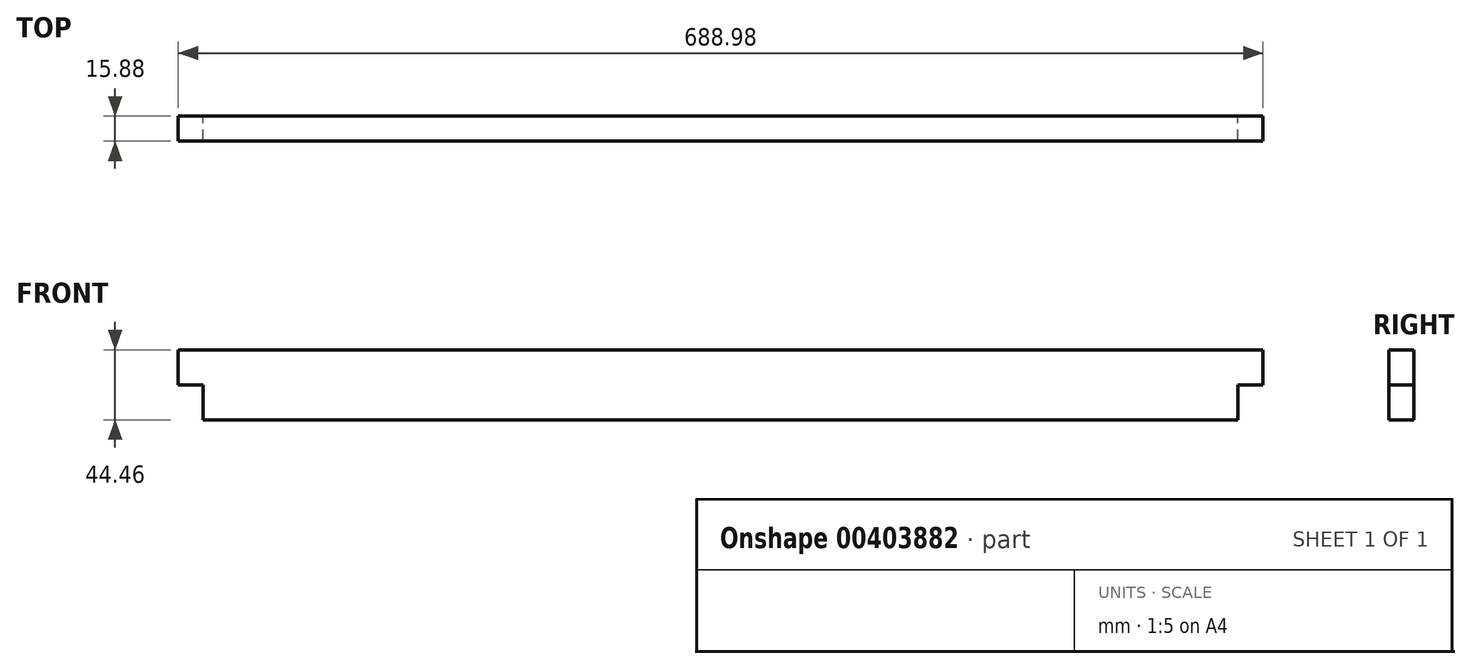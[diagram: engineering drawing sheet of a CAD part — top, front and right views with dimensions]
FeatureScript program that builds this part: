
annotation { "Feature Type Name" : "Feature", "Feature Type Description" : "" }
export const myFeature = defineFeature(function(context is Context, id is Id, definition is map)
    precondition{}
    {
        {
            var Q0;
            Q0=qCreatedBy(makeId("Front.planeOp"),FACE);
            var sketch = newSketch(context, id + "F0", { "sketchPlane" : qUnion([Q0])});
            skLineSegment(sketch, "E0.bottom", {"start": v(344.49, -22.23) * mm, "end": v(-344.49, -22.23) * mm});
            skLineSegment(sketch, "E0.top", {"start": v(344.49, 22.23) * mm, "end": v(-344.49, 22.22) * mm});
            skLineSegment(sketch, "E0.left", {"start": v(344.49, -22.23) * mm, "end": v(344.49, 22.22) * mm});
            skLineSegment(sketch, "E0.right", {"start": v(-344.49, -22.23) * mm, "end": v(-344.49, 22.22) * mm});
            skPoint(sketch, "E0.middle", {"position": v(0, 0) * mm});
            skSolve(sketch);
        }
        {
            var Q0;
            Q0 = qSketchRegion(id + "F0", true);
            extrude(context, id + "F1", {"entities" : qUnion([Q0]), "depth" : 15.88 * mm});
        }
        {
            var Q0;
            Q0=makeQuery(id+"F0.imprint","IMPRINT",FACE,{"disambiguationData":[TD([[makeQuery(id+"F0.imprint","IMPRINT",EDGE,{"derivedFrom":sQuery(id+"F0.wireOp",EDGE,"E0.bottom")}),-1.0]])]});
            var sketch = newSketch(context, id + "F2", { "sketchPlane" : qUnion([Q0])});
            skLineSegment(sketch, "E1.bottom", {"start": v(-344.49, -22.23) * mm, "end": v(-328.61, -22.23) * mm});
            skLineSegment(sketch, "E1.top", {"start": v(-344.49, 0) * mm, "end": v(-328.61, 0) * mm});
            skLineSegment(sketch, "E1.left", {"start": v(-344.49, -22.23) * mm, "end": v(-344.49, 0) * mm});
            skLineSegment(sketch, "E1.right", {"start": v(-328.61, -22.23) * mm, "end": v(-328.61, 0) * mm});
            skLineSegment(sketch, "E2.MirrorCS", {"start": v(328.61, -22.23) * mm, "end": v(328.61, 0) * mm});
            skLineSegment(sketch, "E3.MirrorCS", {"start": v(344.49, -22.23) * mm, "end": v(344.49, 0) * mm});
            skLineSegment(sketch, "E4.MirrorCS", {"start": v(344.49, -22.23) * mm, "end": v(328.61, -22.23) * mm});
            skLineSegment(sketch, "E5.MirrorCS", {"start": v(344.49, 0) * mm, "end": v(328.61, 0) * mm});
            skSolve(sketch);
        }
        {
            var Q0;
            Q0 = qSketchRegion(id + "F2", true);
            extrude(context, id + "F3", {"entities" : qUnion([Q0]), "operationType" : NewBodyOperationType.REMOVE, "endBound" : BoundingType.THROUGH_ALL, "depth" : 25.4 * mm});
        }
    });
